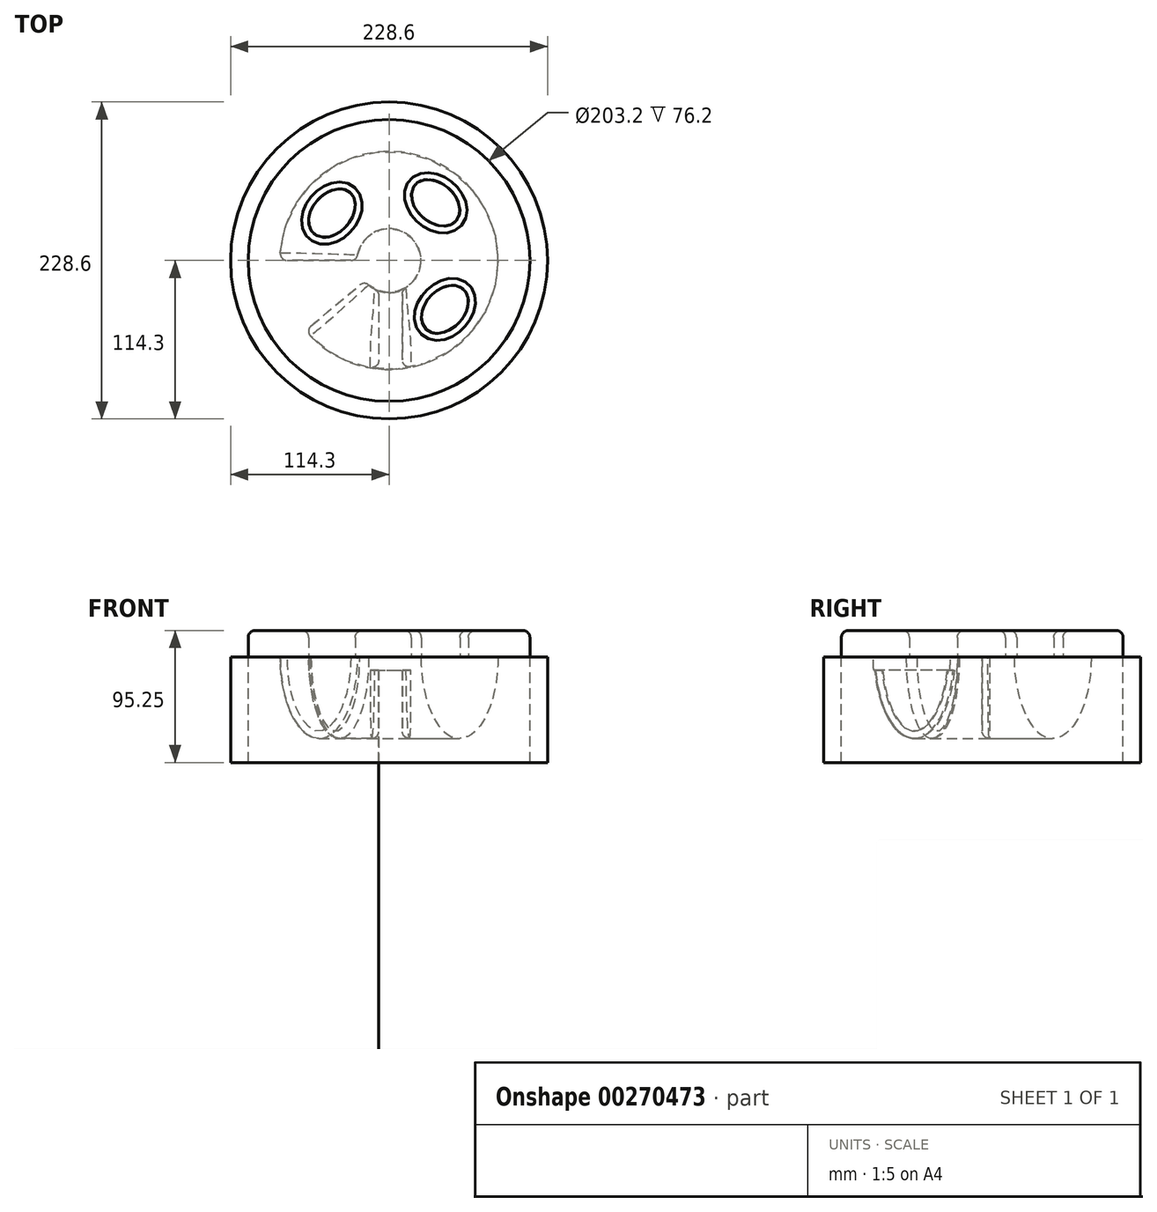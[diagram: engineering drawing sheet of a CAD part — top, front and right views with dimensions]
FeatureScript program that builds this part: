
annotation { "Feature Type Name" : "Feature", "Feature Type Description" : "" }
export const myFeature = defineFeature(function(context is Context, id is Id, definition is map)
    precondition{}
    {
        {
            var Q0;
            Q0=qCreatedBy(makeId("Top.planeOp"),FACE);
            var sketch = newSketch(context, id + "F0", { "sketchPlane" : qUnion([Q0])});
            skCircle(sketch, "E0", {"center": v(0, 0) * mm, "radius": 101.6 * mm});
            skSolve(sketch);
        }
        {
            var Q0;
            Q0 = qSketchRegion(id + "F0", true);
            extrude(context, id + "F1", {"entities" : qUnion([Q0]), "oppositeDirection" : true, "depth" : 76.2 * mm});
        }
        {
            var Q0;
            Q0=qCreatedBy(makeId("Front.planeOp"),FACE);
            var sketch = newSketch(context, id + "F2", { "sketchPlane" : qUnion([Q0])});
            skEllipticalArc(sketch, "E1", {});
            skLineSegment(sketch, "E2", {"start": v(-78.64, 0) * mm, "end": v(-22.96, 0) * mm});
            const initialGuessF2  = {"E1": [-0.0508, 0, 0, 1, 0.05877574533224106, 0.027840361315373166, 1.5707963267948966, 4.71238898038469]};
            skSetInitialGuess(sketch, initialGuessF2);
            skSolve(sketch);
        }
        {
            var Q0;
            Q0 = qSketchRegion(id + "F2", true);
            var Q1;
            Q1=makeQuery(id+"F1.opExtrude","CAP_EDGE",EDGE,{"disambiguationData":[OSD([sQuery(id+"F0.wireOp",EDGE,"E0")])],"isStart":true});
            revolve(context, id + "F3", {"operationType" : NewBodyOperationType.REMOVE, "entities" : qUnion([Q0]), "axis" : qUnion([Q1]), "revolveType" : RevolveType.ONE_DIRECTION, "oppositeDirection" : true, "angle" : 320 * degree});
        }
        {
            var Q0;
            Q0=qCreatedBy(makeId("Top.planeOp"),FACE);
            var sketch = newSketch(context, id + "F4", { "sketchPlane" : qUnion([Q0])});
            skLineSegment(sketch, "E3.bottom", {"start": v(-7.4, -19.41) * mm, "end": v(9.57, -19.41) * mm});
            skLineSegment(sketch, "E3.top", {"start": v(-7.4, -80.8) * mm, "end": v(9.57, -80.8) * mm});
            skLineSegment(sketch, "E3.left", {"start": v(-7.4, -19.41) * mm, "end": v(-7.4, -80.8) * mm});
            skLineSegment(sketch, "E3.right", {"start": v(9.57, -19.41) * mm, "end": v(9.57, -80.8) * mm});
            skSolve(sketch);
        }
        {
            var Q0;
            Q0=makeQuery(id+"F4.imprint","IMPRINT",FACE,{"disambiguationData":[TD([[makeQuery(id+"F4.imprint","IMPRINT",EDGE,{"derivedFrom":sQuery(id+"F4.wireOp",EDGE,"E3.bottom")}),-1.0]])]});
            extrude(context, id + "F5", {"entities" : qUnion([Q0]), "operationType" : NewBodyOperationType.ADD, "oppositeDirection" : true, "depth" : 76.2 * mm, "hasSecondDirection" : true, "secondDirectionOppositeDirection" : true, "secondDirectionDepth" : 9.52 * mm});
        }
        {
            var Q0;
            Q0=qCreatedBy(makeId("Top.planeOp"),FACE);
            var sketch = newSketch(context, id + "F6", { "sketchPlane" : qUnion([Q0])});
            skCircle(sketch, "E4", {"center": v(0, 0) * mm, "radius": 101.6 * mm});
            skEllipse(sketch, "E5", {"center": v(40.29, -35.23) * mm, "majorRadius": 19.75 * mm, "minorRadius": 14.03 * mm, "majorAxis": v(-0.69, -0.73)});
            skEllipse(sketch, "E6.2.0", {"center": v(-41.18, 34.17) * mm, "majorRadius": 19.75 * mm, "minorRadius": 14.03 * mm, "majorAxis": v(0.67, 0.74)});
            skEllipse(sketch, "E6.3.0", {"center": v(33.64, 41.62) * mm, "majorRadius": 19.75 * mm, "minorRadius": 14.03 * mm, "majorAxis": v(0.75, -0.66)});
            skLineSegment(sketch, "E6.anchor1", {"start": v(0, 0) * mm, "end": v(40.29, -35.23) * mm, "construction": true});
            skLineSegment(sketch, "E6.anchor2", {"start": v(0, 0) * mm, "end": v(33.64, 41.62) * mm, "construction": true});
            skSolve(sketch);
        }
        {
            var Q0;
            Q0=makeQuery(id+"F6.imprint","IMPRINT",FACE,{"disambiguationData":[TD([[makeQuery(id+"F6.imprint","IMPRINT",EDGE,{"derivedFrom":sQuery(id+"F6.wireOp",EDGE,"E4")}),1.0]])]});
            extrude(context, id + "F7", {"entities" : qUnion([Q0]), "depth" : 19.05 * mm});
        }
        {
            var Q0;
            {var subQ0=sQuery(id+"F2.wireOp",EDGE,"E2");var subQ1=sQuery(id+"F2.wireOp",EDGE,"E1");Q0=makeQuery(id+"F3.boolean.opBoolean","COPY",EDGE,{"derivedFrom":makeQuery(id+"F3.opRevolve","SWEPT_EDGE",EDGE,{"disambiguationData":[OSD([subQ1,subQ0]),TDD([makeQuery(id+"F2.imprint","INTERSECT",VERTEX,{"disambiguationData":[OD(1.0)],"derivedFrom":[subQ1,subQ0]})])]})});}
            var Q1;
            {var subQ0=sQuery(id+"F2.wireOp",EDGE,"E2");var subQ1=sQuery(id+"F2.wireOp",EDGE,"E1");Q1=makeQuery(id+"F3.boolean.opBoolean","COPY",EDGE,{"derivedFrom":makeQuery(id+"F3.opRevolve","SWEPT_EDGE",EDGE,{"disambiguationData":[OSD([subQ1,subQ0]),TDD([makeQuery(id+"F2.imprint","INTERSECT",VERTEX,{"disambiguationData":[OD(0.0)],"derivedFrom":[subQ1,subQ0]})])]})});}
            var Q2;
            Q2=makeQuery(id+"F3.boolean.opBoolean","COPY",EDGE,{"derivedFrom":makeQuery(id+"F3.opRevolve","CAP_EDGE",EDGE,{"disambiguationData":[OSD([sQuery(id+"F2.wireOp",EDGE,"E1")])],"isStart":true})});
            var Q3;
            Q3=makeQuery(id+"F5.boolean.opBoolean","INTERSECT",EDGE,{"derivedFrom":[makeQuery(id+"F3.boolean.opBoolean","COPY",FACE,{"derivedFrom":makeQuery(id+"F3.opRevolve","SWEPT_FACE",FACE,{"disambiguationData":[OSD([sQuery(id+"F2.wireOp",EDGE,"E1")])]})}),makeQuery(id+"F5.opExtrude","SWEPT_FACE",FACE,{"disambiguationData":[OSD([sQuery(id+"F4.wireOp",EDGE,"E3.right")])]})]});
            var Q4;
            Q4=makeQuery(id+"F3.boolean.opBoolean","COPY",EDGE,{"derivedFrom":makeQuery(id+"F3.opRevolve","CAP_EDGE",EDGE,{"disambiguationData":[OSD([sQuery(id+"F2.wireOp",EDGE,"E1")])],"isStart":false})});
            var Q5;
            Q5=makeQuery(id+"F5.boolean.opBoolean","INTERSECT",EDGE,{"derivedFrom":[makeQuery(id+"F3.boolean.opBoolean","COPY",FACE,{"derivedFrom":makeQuery(id+"F3.opRevolve","SWEPT_FACE",FACE,{"disambiguationData":[OSD([sQuery(id+"F2.wireOp",EDGE,"E1")])]})}),makeQuery(id+"F5.opExtrude","SWEPT_FACE",FACE,{"disambiguationData":[OSD([sQuery(id+"F4.wireOp",EDGE,"E3.left")])]})]});
            fillet(context, id + "F8", {"entities" : qUnion([Q0, Q1, Q2, Q3, Q4, Q5]), "radius" : 5.08 * mm, "tangentPropagation" : true, "allowEdgeOverflow" : false});
        }
        {
            var Q0;
            Q0=makeQuery(id+"F7.opExtrude","CAP_EDGE",EDGE,{"disambiguationData":[OSD([sQuery(id+"F6.wireOp",EDGE,"E6.2.0")])],"isStart":false});
            var Q1;
            Q1=makeQuery(id+"F7.opExtrude","CAP_EDGE",EDGE,{"disambiguationData":[OSD([sQuery(id+"F6.wireOp",EDGE,"E6.3.0")])],"isStart":false});
            var Q2;
            Q2=makeQuery(id+"F7.opExtrude","CAP_EDGE",EDGE,{"disambiguationData":[OSD([sQuery(id+"F6.wireOp",EDGE,"E5")])],"isStart":false});
            var Q3;
            Q3=makeQuery(id+"F7.opExtrude","CAP_EDGE",EDGE,{"disambiguationData":[OSD([sQuery(id+"F6.wireOp",EDGE,"E4")])],"isStart":false});
            fillet(context, id + "F9", {"entities" : qUnion([Q0, Q1, Q2, Q3]), "radius" : 5.08 * mm, "tangentPropagation" : true, "allowEdgeOverflow" : false});
        }
        {
            var Q0;
            Q0=makeQuery(id+"F6.imprint","IMPRINT",FACE,{"disambiguationData":[TD([[makeQuery(id+"F6.imprint","IMPRINT",EDGE,{"derivedFrom":sQuery(id+"F6.wireOp",EDGE,"E4")}),1.0]])]});
            var sketch = newSketch(context, id + "F10", { "sketchPlane" : qUnion([Q0])});
            skCircle(sketch, "E7", {"center": v(0, 0) * mm, "radius": 114.3 * mm});
            skSolve(sketch);
        }
        {
            var Q0;
            Q0 = qSketchRegion(id + "F10", true);
            extrude(context, id + "F11", {"entities" : qUnion([Q0]), "oppositeDirection" : true, "depth" : 76.2 * mm});
        }
        {
            var Q0;
            Q0=makeQuery(id+"F1.opExtrude","SWEPT_BODY",BODY,{"disambiguationData":[OSD([sQuery(id+"F0.wireOp",EDGE,"E0")])]});
            var Q1;
            Q1=makeQuery(id+"F11.opExtrude","SWEPT_BODY",BODY,{"disambiguationData":[OSD([sQuery(id+"F10.wireOp",EDGE,"E7")])]});
            booleanBodies(context, id + "F12", {"operationType" : BooleanOperationType.SUBTRACTION, "tools" : qUnion([Q0]), "targets" : qUnion([Q1]), "keepTools" : true});
        }
    });
